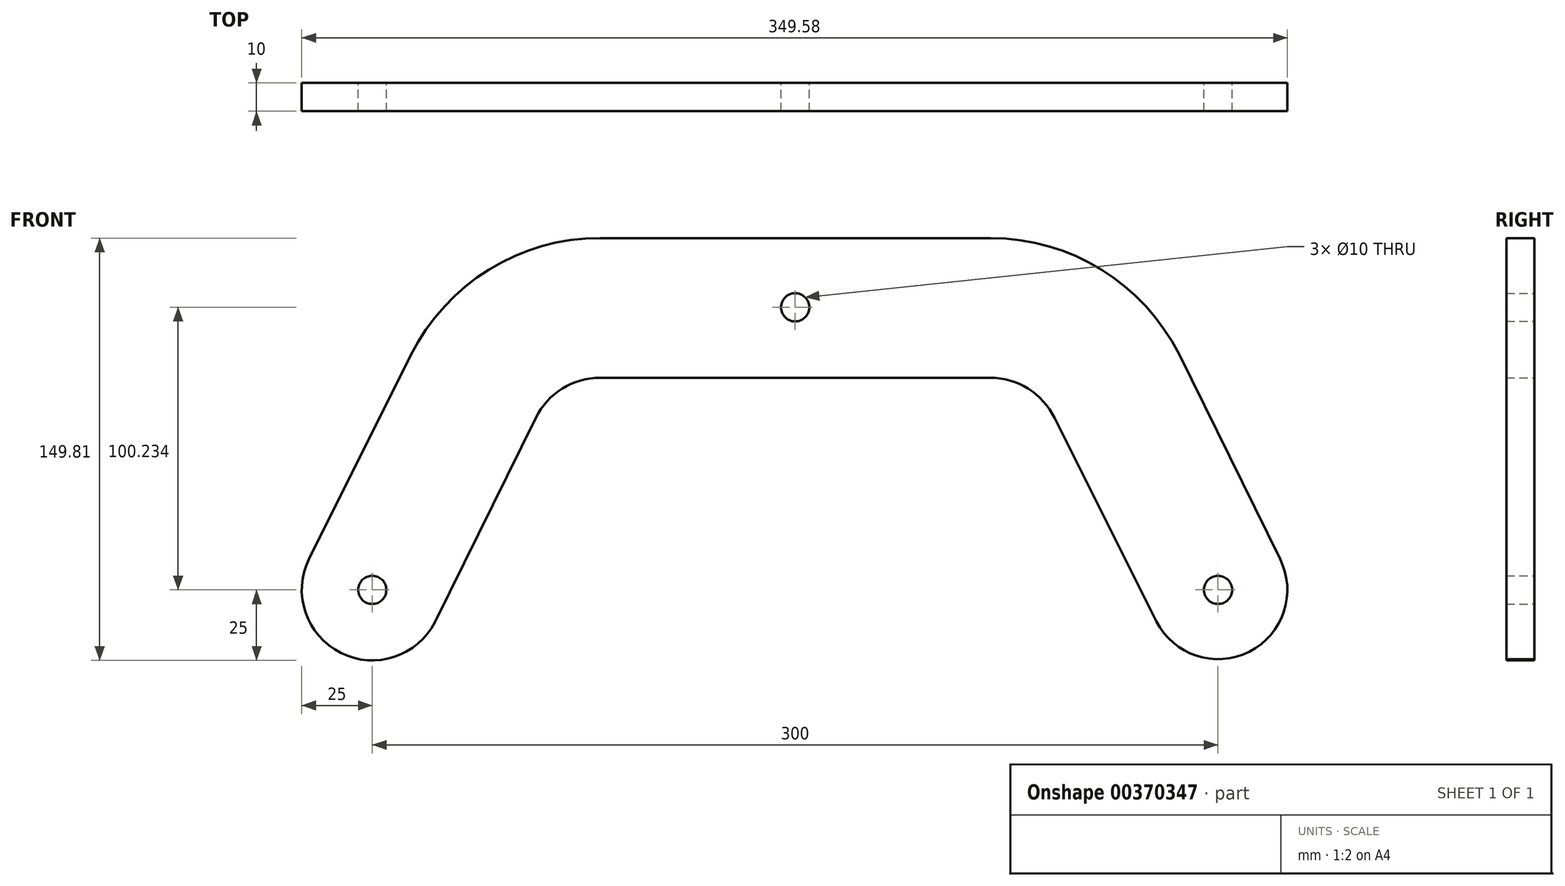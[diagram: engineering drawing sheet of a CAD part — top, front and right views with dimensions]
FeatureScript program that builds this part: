
annotation { "Feature Type Name" : "Feature", "Feature Type Description" : "" }
export const myFeature = defineFeature(function(context is Context, id is Id, definition is map)
    precondition{}
    {
        {
            var Q0;
            Q0=qCreatedBy(makeId("Front.planeOp"),FACE);
            var sketch = newSketch(context, id + "F0", { "sketchPlane" : qUnion([Q0])});
            skLineSegment(sketch, "E0", {"start": v(-286.18, 133.54) * mm, "end": v(-322.42, 61.06) * mm});
            skLineSegment(sketch, "E1", {"start": v(-219.16, 174.81) * mm, "end": v(-80.52, 174.81) * mm});
            skLineSegment(sketch, "E2", {"start": v(21.99, 61) * mm, "end": v(-13.82, 133.54) * mm});
            skLineSegment(sketch, "E3", {"start": v(-21.9, 38.82) * mm, "end": v(-58.17, 111.38) * mm});
            skPoint(sketch, "E4.MirrorCS.start.orphan", {"position": v(-250, 150) * mm});
            skPoint(sketch, "E5.end.orphan", {"position": v(-300, 50) * mm});
            skLineSegment(sketch, "E6.trimOffspring", {"start": v(-277.58, 38.94) * mm, "end": v(-277.7, 38.7) * mm});
            skPoint(sketch, "E7.trimOffspring.end.orphan", {"position": v(-93.97, 128.02) * mm});
            skPoint(sketch, "E8.end.orphan", {"position": v(-50, 150) * mm});
            skArc(sketch, "E9", {"start": v(-322.42, 61.06) * mm, "mid": v(-311.06, 27.58) * mm, "end": v(-277.58, 38.94) * mm});
            skArc(sketch, "E10", {"start": v(-21.9, 38.82) * mm, "mid": v(11.09, 28.06) * mm, "end": v(21.99, 61) * mm});
            skArc(sketch, "E11", {"start": v(-57.97, 110.98) * mm, "mid": v(-58.07, 111.18) * mm, "end": v(-58.17, 111.38) * mm});
            skArc(sketch, "E12", {"start": v(-13.82, 133.54) * mm, "mid": v(-41.35, 163.6) * mm, "end": v(-80.52, 174.81) * mm});
            skPoint(sketch, "E13.MirrorCS.start.orphan", {"position": v(-43.97, 28.02) * mm});
            skLineSegment(sketch, "E14", {"start": v(-277.58, 38.94) * mm, "end": v(-242, 111.03) * mm});
            skArc(sketch, "E15", {"start": v(-58.17, 111.38) * mm, "mid": v(-67.54, 121.5) * mm, "end": v(-80.8, 125.23) * mm});
            skLineSegment(sketch, "E16", {"start": v(-80.8, 125.23) * mm, "end": v(-219.16, 125.23) * mm});
            skPoint(sketch, "E17.MirrorCS.end.orphan", {"position": v(-254.84, 27.45) * mm});
            skPoint(sketch, "E18.trimOffspring.end.orphan", {"position": v(-219.16, 99.81) * mm});
            skPoint(sketch, "E19.end.orphan", {"position": v(-254.84, 27.74) * mm});
            skArc(sketch, "E20", {"start": v(-219.16, 125.23) * mm, "mid": v(-232.6, 121.4) * mm, "end": v(-242, 111.03) * mm});
            skArc(sketch, "E21", {"start": v(-219.16, 174.81) * mm, "mid": v(-258.62, 163.6) * mm, "end": v(-286.29, 133.33) * mm});
            skCircle(sketch, "E22", {"center": v(-300, 50) * mm, "radius": 5 * mm});
            skCircle(sketch, "E23", {"center": v(0, 50) * mm, "radius": 5 * mm});
            skCircle(sketch, "E24", {"center": v(-150, 150.23) * mm, "radius": 5 * mm});
            skSolve(sketch);
        }
        {
            var Q0;
            Q0=makeQuery(id+"F0.imprint","IMPRINT",FACE,{"disambiguationData":[TD([[makeQuery(id+"F0.imprint","IMPRINT",EDGE,{"derivedFrom":sQuery(id+"F0.wireOp",EDGE,"E1")}),-1.0]])]});
            extrude(context, id + "F1", {"entities" : qUnion([Q0]), "depth" : 10 * mm});
        }
    });
